# Revit family: revitupgrade
name_source: partatom
category: Furniture
units: mm (PartAtom-declared; Revit-internal decimal feet)

## family parameters
Always vertical = Yes
Cut with Voids When Loaded = No
Enable Cutting in Views = No
Render Appearance Source = Family Geometry
Room Calculation Point = No
Shared = No
Work Plane-Based = No

## types (20) — shared parameters
Assembly Code = E2020200
Base Option 1 = Steelcase_AP_Desking_HeightAdjustable_MigrationSEPro_Base_Desk : Fix Height
Base Option 2 = Steelcase_AP_Desking_HeightAdjustable_MigrationSEPro_Base_Desk : Basic Height
Base Option 3 = Steelcase_AP_Desking_HeightAdjustable_MigrationSEPro_Base_Desk : Extended Height
Default Elevation = 0.00 mm
Manufacturer = Steelcase
Product = Desking
Product Line = Migration SE Pro
Release Date = February 2020
Style Number(s) = MGDFLRQB, MGDBLRQB, MGDELRQB, MGDEWSRQ
URL = https://www.steelcase.com

## per-type parameters (varying)
| type | Column Position | Depth | Width |
| 700D x 1400W | 375.00 mm | 700.00 mm | 1400.00 mm |
| 750D x 1200W | 400.00 mm | 750.00 mm | 1200.00 mm |
| 800D x 1200W | 425.00 mm | 800.00 mm | 1200.00 mm |
| 900D x 1200W | 475.00 mm | 900.00 mm | 1200.00 mm |
| 700D x 1200W | 375.00 mm | 700.00 mm | 1200.00 mm |
| 700D x 1500W | 375.00 mm | 700.00 mm | 1500.00 mm |
| 700D x 1600W | 375.00 mm | 700.00 mm | 1600.00 mm |
| 700D x 1800W | 375.00 mm | 700.00 mm | 1800.00 mm |
| 750D x 1400W | 400.00 mm | 750.00 mm | 1400.00 mm |
| 750D x 1500W | 400.00 mm | 750.00 mm | 1500.00 mm |
| 750D x 1600W | 400.00 mm | 750.00 mm | 1600.00 mm |
| 750D x 1800W | 400.00 mm | 750.00 mm | 1800.00 mm |
| 800D x 1400W | 425.00 mm | 800.00 mm | 1400.00 mm |
| 800D x 1500W | 425.00 mm | 800.00 mm | 1500.00 mm |
| 800D x 1600W | 425.00 mm | 800.00 mm | 1600.00 mm |
| 800D x 1800W | 425.00 mm | 800.00 mm | 1800.00 mm |
| 900D x 1400W | 475.00 mm | 900.00 mm | 1400.00 mm |
| 900D x 1500W | 475.00 mm | 900.00 mm | 1500.00 mm |
| 900D x 1600W | 475.00 mm | 900.00 mm | 1600.00 mm |
| 900D x 1800W | 475.00 mm | 900.00 mm | 1800.00 mm |

## geometry (parser evidence)
native form markers: Sweep x7
no freeform markers — native parametric forms only
